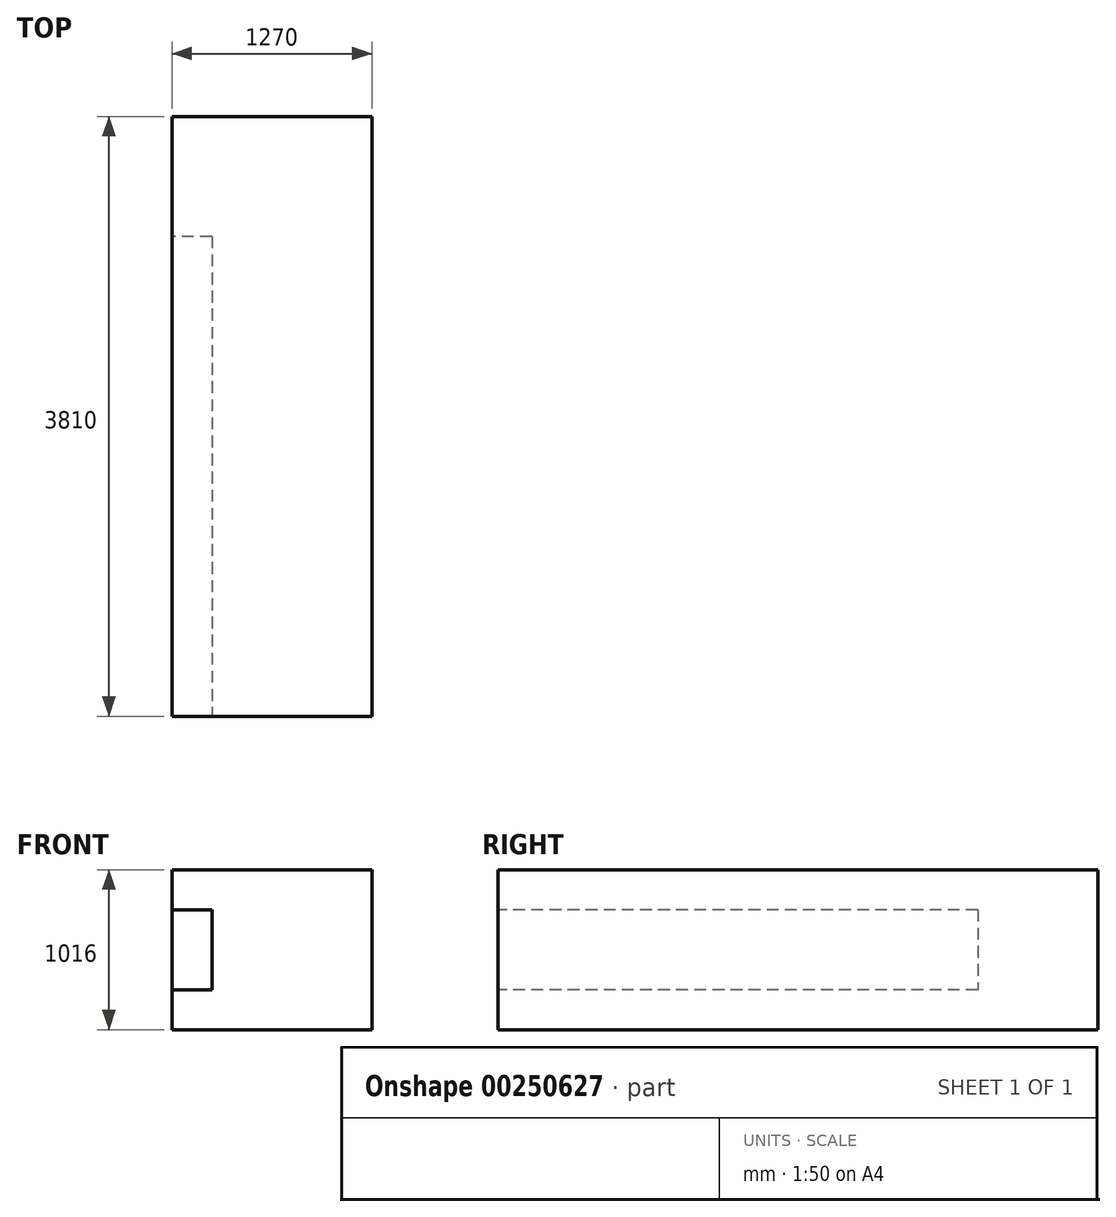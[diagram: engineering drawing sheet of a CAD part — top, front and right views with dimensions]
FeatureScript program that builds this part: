
annotation { "Feature Type Name" : "Feature", "Feature Type Description" : "" }
export const myFeature = defineFeature(function(context is Context, id is Id, definition is map)
    precondition{}
    {
        {
            var Q0;
            Q0=qCreatedBy(makeId("Front.planeOp"),FACE);
            var sketch = newSketch(context, id + "F0", { "sketchPlane" : qUnion([Q0])});
            skLineSegment(sketch, "E0.bottom", {"start": v(-636.65, 639.53) * mm, "end": v(633.35, 639.53) * mm});
            skLineSegment(sketch, "E0.top", {"start": v(-636.65, -376.47) * mm, "end": v(633.35, -376.47) * mm});
            skLineSegment(sketch, "E0.left", {"start": v(-636.65, 639.53) * mm, "end": v(-636.65, -376.47) * mm});
            skLineSegment(sketch, "E0.right", {"start": v(633.35, 639.53) * mm, "end": v(633.35, -376.47) * mm});
            skSolve(sketch);
        }
        {
            var Q0;
            Q0 = qSketchRegion(id + "F0", true);
            extrude(context, id + "F1", {"entities" : qUnion([Q0]), "depth" : 3810 * mm});
        }
        {
            var Q0;
            Q0=makeQuery(id+"F1.opExtrude","SWEPT_FACE",FACE,{"disambiguationData":[OSD([sQuery(id+"F0.wireOp",EDGE,"E0.left")])]});
            var sketch = newSketch(context, id + "F2", { "sketchPlane" : qUnion([Q0])});
            skLineSegment(sketch, "E1.bottom", {"start": v(762, 385.53) * mm, "end": v(3810, 385.53) * mm});
            skLineSegment(sketch, "E1.top", {"start": v(762, -122.47) * mm, "end": v(3810, -122.47) * mm});
            skLineSegment(sketch, "E1.left", {"start": v(762, 385.53) * mm, "end": v(762, -122.47) * mm});
            skLineSegment(sketch, "E1.right", {"start": v(3810, 385.53) * mm, "end": v(3810, -122.47) * mm});
            skSolve(sketch);
        }
        {
            var Q0;
            Q0=makeQuery(id+"F2.imprint","IMPRINT",FACE,{"disambiguationData":[TD([[makeQuery(id+"F2.imprint","IMPRINT",EDGE,{"derivedFrom":sQuery(id+"F2.wireOp",EDGE,"E1.bottom")}),-1.0]])]});
            extrude(context, id + "F3", {"entities" : qUnion([Q0]), "oppositeDirection" : true, "depth" : 254 * mm});
        }
        {
            var Q0;
            Q0=makeQuery(id+"F3.opExtrude","SWEPT_BODY",BODY,{"disambiguationData":[OSD([sQuery(id+"F2.wireOp",EDGE,"E1.bottom"),sQuery(id+"F2.wireOp",EDGE,"E1.top"),sQuery(id+"F2.wireOp",EDGE,"E1.left"),sQuery(id+"F2.wireOp",EDGE,"E1.right")])]});
            var Q1;
            Q1=makeQuery(id+"F1.opExtrude","SWEPT_BODY",BODY,{"disambiguationData":[OSD([sQuery(id+"F0.wireOp",EDGE,"E0.bottom"),sQuery(id+"F0.wireOp",EDGE,"E0.top"),sQuery(id+"F0.wireOp",EDGE,"E0.left"),sQuery(id+"F0.wireOp",EDGE,"E0.right")])]});
            booleanBodies(context, id + "F4", {"operationType" : BooleanOperationType.SUBTRACTION, "tools" : qUnion([Q0]), "targets" : qUnion([Q1])});
        }
    });
